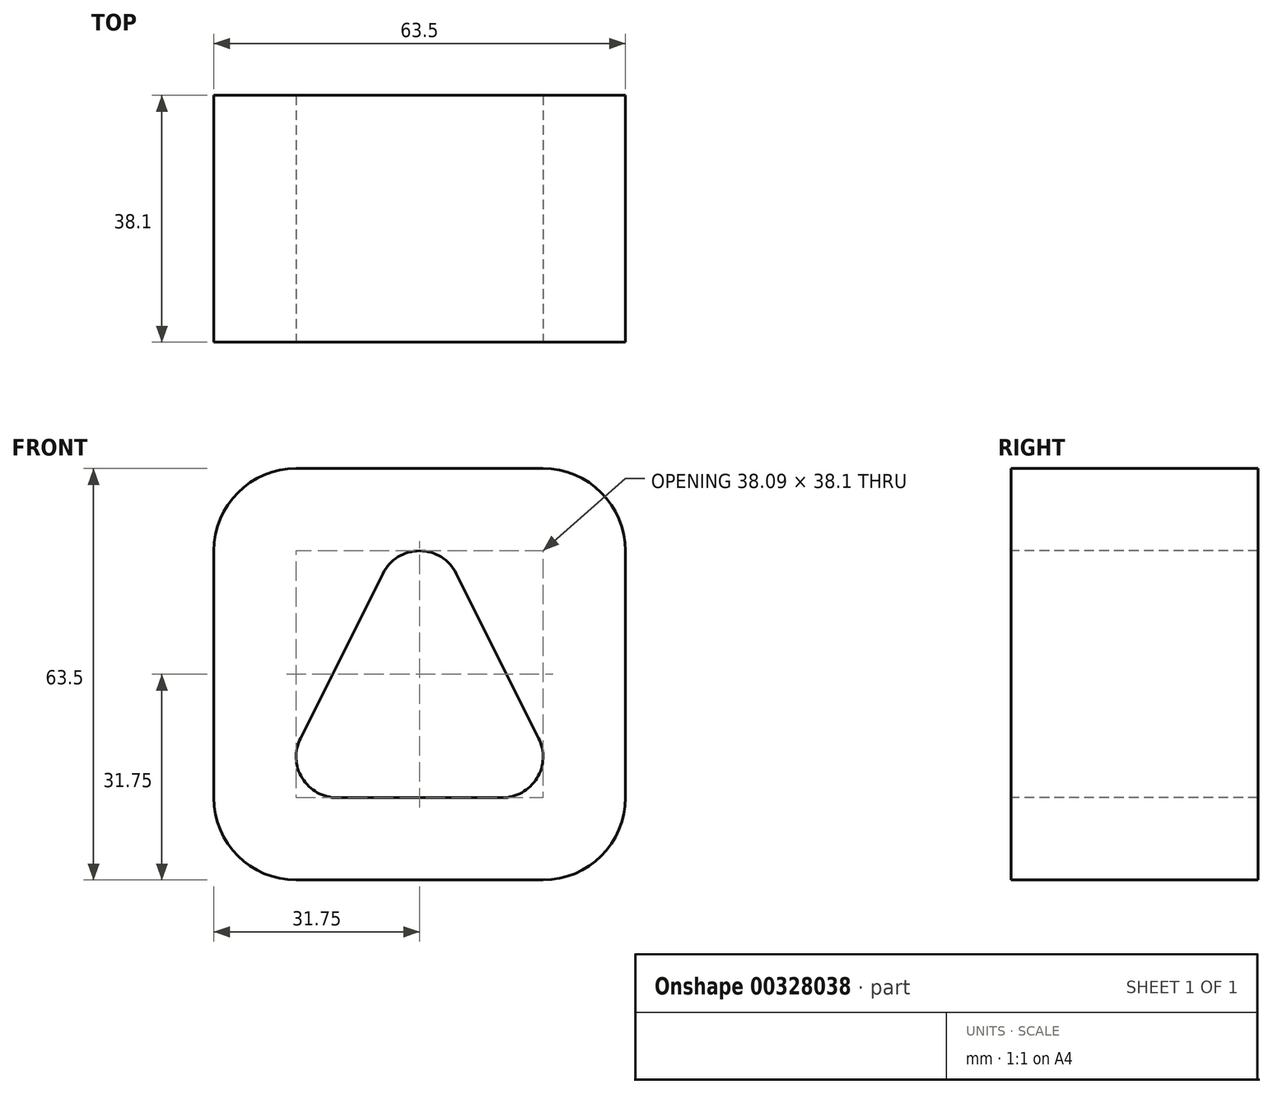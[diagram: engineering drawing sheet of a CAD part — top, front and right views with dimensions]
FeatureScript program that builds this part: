
annotation { "Feature Type Name" : "Feature", "Feature Type Description" : "" }
export const myFeature = defineFeature(function(context is Context, id is Id, definition is map)
    precondition{}
    {
        {
            var Q0;
            Q0=qCreatedBy(makeId("Front.planeOp"),FACE);
            var sketch = newSketch(context, id + "F0", { "sketchPlane" : qUnion([Q0])});
            skLineSegment(sketch, "E0", {"start": v(0, 63.5) * mm, "end": v(0, 63.5) * mm});
            skLineSegment(sketch, "E1", {"start": v(0, 0) * mm, "end": v(0, 0) * mm});
            skLineSegment(sketch, "E2", {"start": v(0, 63.5) * mm, "end": v(63.5, 63.5) * mm});
            skLineSegment(sketch, "E3", {"start": v(63.5, 63.5) * mm, "end": v(63.5, 0) * mm});
            skLineSegment(sketch, "E4", {"start": v(63.5, 0) * mm, "end": v(0, 0) * mm});
            skLineSegment(sketch, "E5", {"start": v(0, 63.5) * mm, "end": v(0, 0) * mm});
            skArc(sketch, "E6", {"start": v(13.37, 21.89) * mm, "mid": v(13.65, 15.71) * mm, "end": v(19.05, 12.7) * mm});
            skArc(sketch, "E7", {"start": v(44.45, 12.7) * mm, "mid": v(49.85, 15.71) * mm, "end": v(50.13, 21.89) * mm});
            skArc(sketch, "E8", {"start": v(37.43, 47.29) * mm, "mid": v(31.75, 50.8) * mm, "end": v(26.07, 47.29) * mm});
            skLineSegment(sketch, "E9", {"start": v(37.43, 47.29) * mm, "end": v(50.13, 21.89) * mm});
            skLineSegment(sketch, "E10", {"start": v(44.45, 12.7) * mm, "end": v(18.93, 12.7) * mm});
            skLineSegment(sketch, "E11", {"start": v(13.37, 21.89) * mm, "end": v(26.07, 47.29) * mm});
            skSolve(sketch);
        }
        {
            var Q0;
            Q0=makeQuery(id+"F0.imprint","IMPRINT",FACE,{"disambiguationData":[TD([[makeQuery(id+"F0.imprint","IMPRINT",EDGE,{"derivedFrom":sQuery(id+"F0.wireOp",EDGE,"E2")}),-1.0]])]});
            extrude(context, id + "F1", {"entities" : qUnion([Q0]), "oppositeDirection" : true, "depth" : 38.1 * mm});
        }
        {
            var Q0;
            Q0=makeQuery(id+"F1.opExtrude","SWEPT_EDGE",EDGE,{"disambiguationData":[OSD([sQuery(id+"F0.wireOp",EDGE,"E2"),sQuery(id+"F0.wireOp",EDGE,"E5")])]});
            var Q1;
            Q1=makeQuery(id+"F1.opExtrude","SWEPT_EDGE",EDGE,{"disambiguationData":[OSD([sQuery(id+"F0.wireOp",EDGE,"E2"),sQuery(id+"F0.wireOp",EDGE,"E3")])]});
            var Q2;
            Q2=makeQuery(id+"F1.opExtrude","SWEPT_EDGE",EDGE,{"disambiguationData":[OSD([sQuery(id+"F0.wireOp",EDGE,"E4"),sQuery(id+"F0.wireOp",EDGE,"E5")])]});
            var Q3;
            Q3=makeQuery(id+"F1.opExtrude","SWEPT_EDGE",EDGE,{"disambiguationData":[OSD([sQuery(id+"F0.wireOp",EDGE,"E3"),sQuery(id+"F0.wireOp",EDGE,"E4")])]});
            fillet(context, id + "F2", {"entities" : qUnion([Q0, Q1, Q2, Q3]), "radius" : 12.7 * mm, "tangentPropagation" : true, "allowEdgeOverflow" : false});
        }
    });
